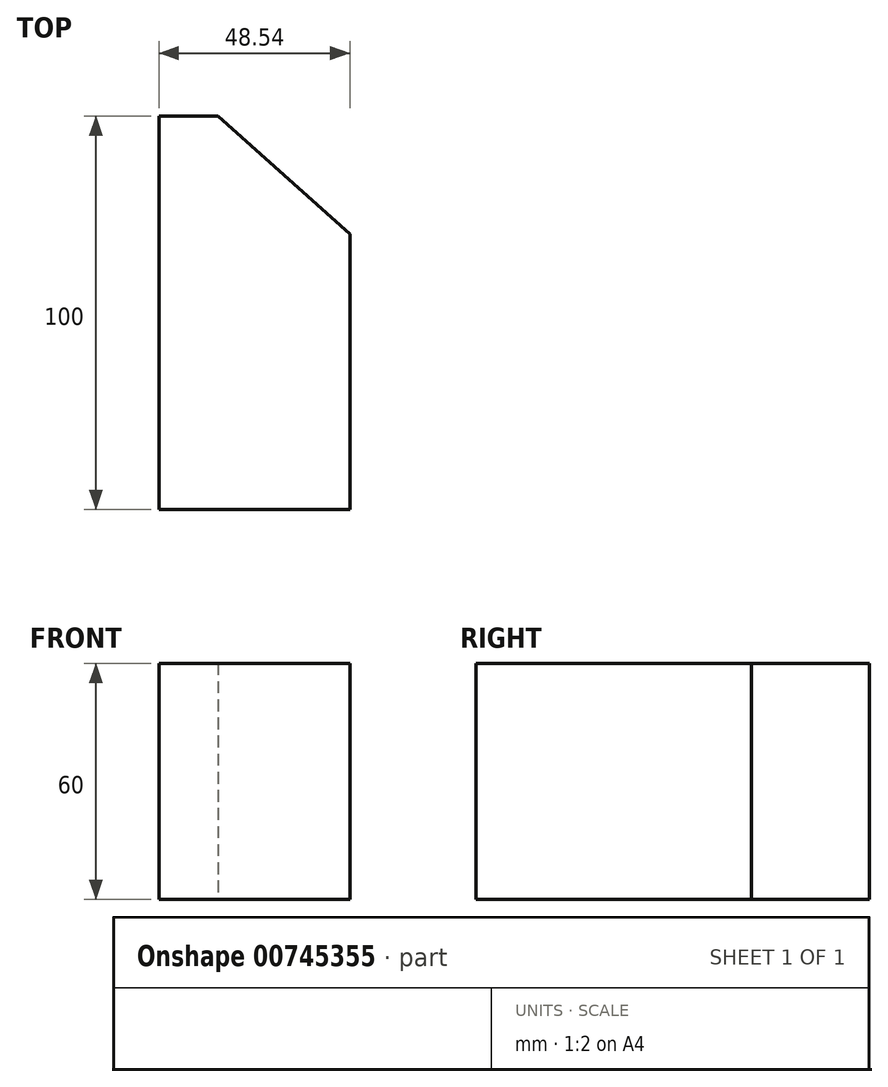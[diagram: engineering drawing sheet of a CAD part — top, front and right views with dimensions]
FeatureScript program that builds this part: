
annotation { "Feature Type Name" : "Feature", "Feature Type Description" : "" }
export const myFeature = defineFeature(function(context is Context, id is Id, definition is map)
    precondition{}
    {
        {
            var Q0;
            Q0=qCreatedBy(makeId("Top.planeOp"),FACE);
            var sketch = newSketch(context, id + "F0", { "sketchPlane" : qUnion([Q0])});
            skLineSegment(sketch, "E0", {"start": v(0, 0) * mm, "end": v(-48.54, 0) * mm});
            skLineSegment(sketch, "E1", {"start": v(-48.54, 0) * mm, "end": v(-48.54, 100) * mm});
            skLineSegment(sketch, "E2", {"start": v(-48.54, 100) * mm, "end": v(-33.54, 100) * mm});
            skLineSegment(sketch, "E3", {"start": v(-33.54, 100) * mm, "end": v(0, 70) * mm});
            skLineSegment(sketch, "E4", {"start": v(0, 70) * mm, "end": v(0, 0) * mm});
            skSolve(sketch);
        }
        {
            var Q0;
            Q0=makeQuery(id+"F0.imprint","IMPRINT",FACE,{"disambiguationData":[TD([[makeQuery(id+"F0.imprint","IMPRINT",EDGE,{"derivedFrom":sQuery(id+"F0.wireOp",EDGE,"E0")}),-1.0]])]});
            extrude(context, id + "F1", {"entities" : qUnion([Q0]), "depth" : 60 * mm, "offsetDistance" : 25 * mm});
        }
    });
